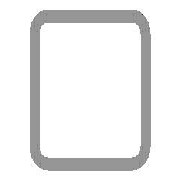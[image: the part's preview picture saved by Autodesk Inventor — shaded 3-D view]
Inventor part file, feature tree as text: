
AUTODESK INVENTOR PART (.ipt)
format: ipt  version: 2025 (Build 290162010, 162A)  size: 134,144 bytes
history: native  units: mm (DEFAULTED — no unit token found)
features: other x4, sketch x1, plane x1
ambient origin geometry x8: Origin, YZ Plane, XZ Plane, XY Plane, X Axis, Y Axis, Z Axis, Center Point
bodies: Solid1 (feature_tree), Body (feature_tree)
feature tree (6):
  parser-record x1  (decoder bookkeeping rows leaked as tree rows — omitted from the tree; the rows remain in map.json)
  other  "Driven Length"
  other  "Start Plane"
  other  "End Plane"
  sketch  "Sketch3"  dims[d3=2200.0mm d4=0.0mm d7=4.0mm d9=40.0mm d11=40.0mm d12=2.0mm d13=-0.0mm d14=2200.0mm d15=20.0mm d16=20.0mm d17=90.0deg d18=2200.0mm]
  plane  "Work Plane3"
